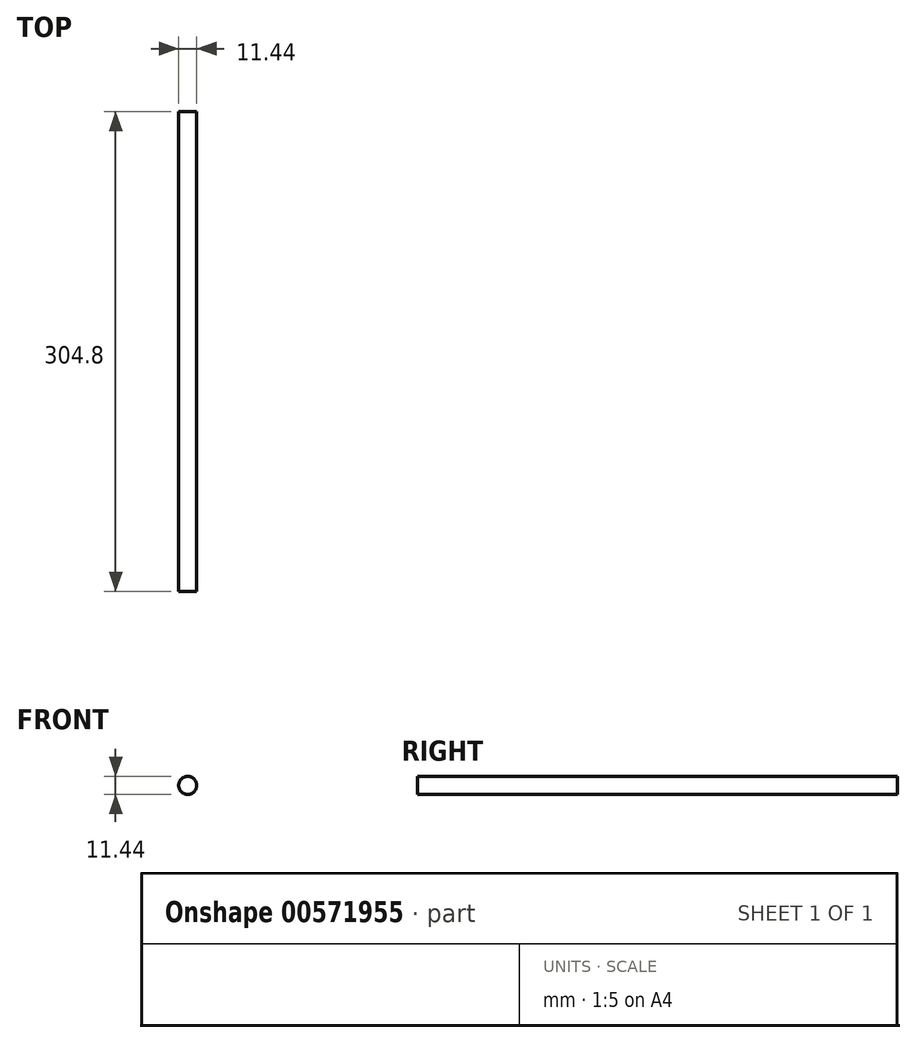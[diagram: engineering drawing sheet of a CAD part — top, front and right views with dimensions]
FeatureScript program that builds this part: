
annotation { "Feature Type Name" : "Feature", "Feature Type Description" : "" }
export const myFeature = defineFeature(function(context is Context, id is Id, definition is map)
    precondition{}
    {
        {
            var Q0;
            Q0=qCreatedBy(makeId("Front.planeOp"),FACE);
            var sketch = newSketch(context, id + "F0", { "sketchPlane" : qUnion([Q0])});
            skCircle(sketch, "E0", {"center": v(0, 0) * mm, "radius": 5.72 * mm});
            skSolve(sketch);
        }
        {
            var Q0;
            Q0 = qSketchRegion(id + "F0", true);
            extrude(context, id + "F1", {"entities" : qUnion([Q0]), "depth" : 304.8 * mm, "offsetDistance" : 25.4 * mm});
        }
    });
